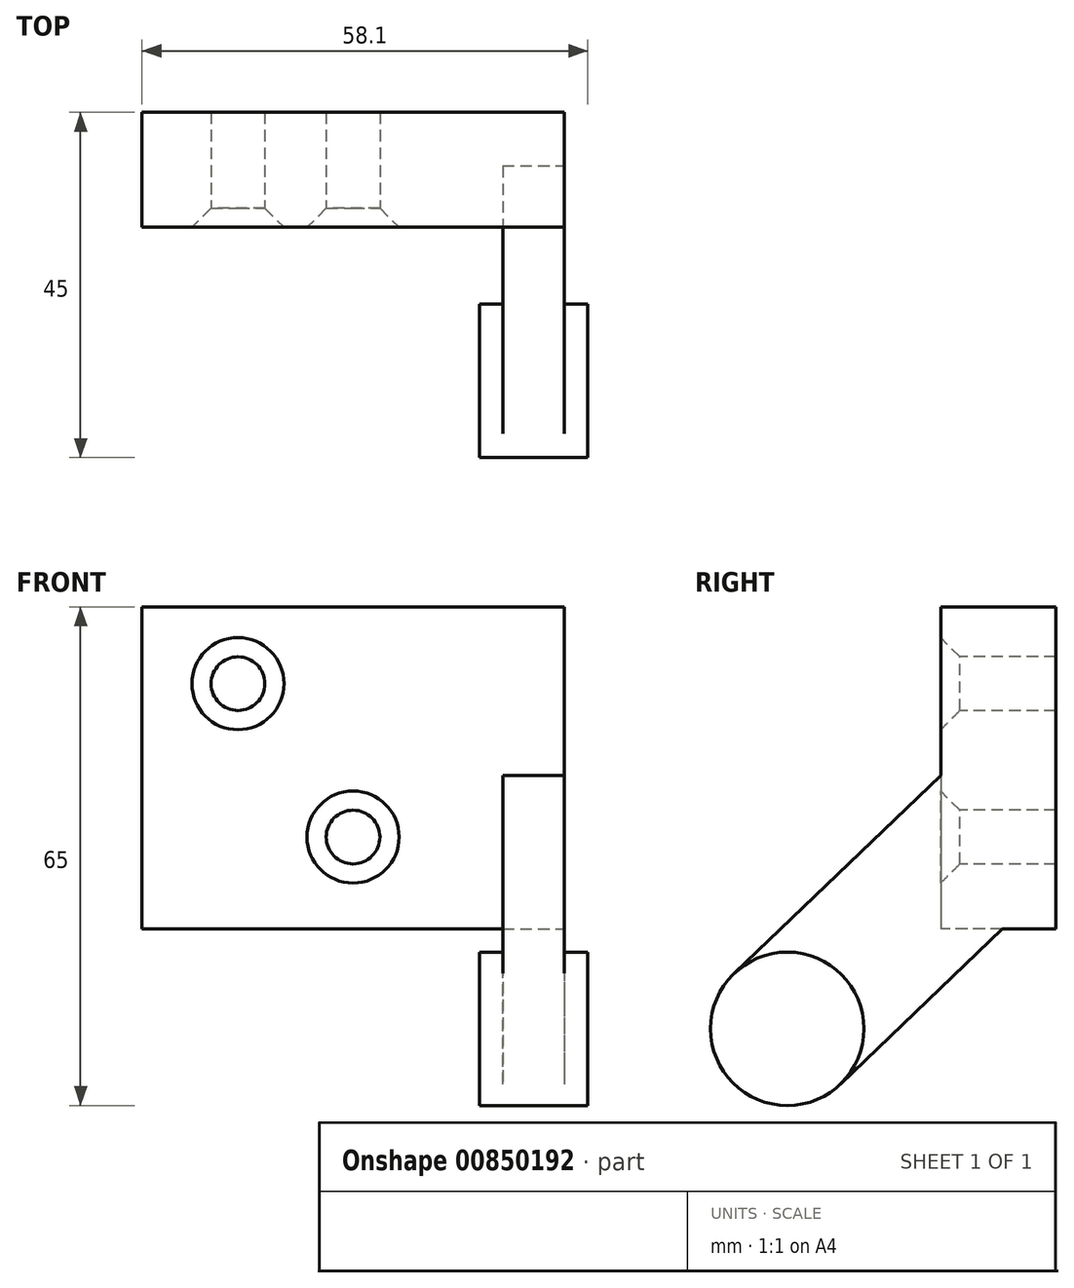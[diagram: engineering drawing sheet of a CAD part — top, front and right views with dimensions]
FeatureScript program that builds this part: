
annotation { "Feature Type Name" : "Feature", "Feature Type Description" : "" }
export const myFeature = defineFeature(function(context is Context, id is Id, definition is map)
    precondition{}
    {
        {
            var Q0;
            Q0=qCreatedBy(makeId("Front.planeOp"),FACE);
            var sketch = newSketch(context, id + "F0", { "sketchPlane" : qUnion([Q0])});
            skLineSegment(sketch, "E0.bottom", {"start": v(-27.5, 0) * mm, "end": v(27.5, 0) * mm});
            skLineSegment(sketch, "E0.top", {"start": v(-27.5, -42) * mm, "end": v(27.5, -42) * mm});
            skLineSegment(sketch, "E0.left", {"start": v(-27.5, 0) * mm, "end": v(-27.5, -42) * mm});
            skLineSegment(sketch, "E0.right", {"start": v(27.5, 0) * mm, "end": v(27.5, -42) * mm});
            skSolve(sketch);
        }
        {
            var Q0;
            Q0=makeQuery(id+"F0.imprint","IMPRINT",FACE,{"disambiguationData":[TD([[makeQuery(id+"F0.imprint","IMPRINT",EDGE,{"derivedFrom":sQuery(id+"F0.wireOp",EDGE,"E0.bottom")}),-1.0]])]});
            var Q1;
            Q1=sQuery(id+"F0.wireOp",EDGE,"E0.right");
            extrude(context, id + "F1", {"entities" : qUnion([Q0]), "surfaceEntities" : qUnion([Q1]), "oppositeDirection" : true, "depth" : 15 * mm, "offsetDistance" : 25 * mm});
        }
        {
            var Q0;
            Q0=makeQuery(id+"F1.opExtrude","SWEPT_FACE",FACE,{"disambiguationData":[OSD([sQuery(id+"F0.wireOp",EDGE,"E0.right")])]});
            var sketch = newSketch(context, id + "F2", { "sketchPlane" : qUnion([Q0])});
            skLineSegment(sketch, "E1", {"start": v(0, -21.96) * mm, "end": v(-26.92, -47.78) * mm});
            skLineSegment(sketch, "E2", {"start": v(8, -42) * mm, "end": v(-13.08, -62.22) * mm});
            skLineSegment(sketch, "E3", {"start": v(-26.92, -47.78) * mm, "end": v(-13.08, -62.22) * mm});
            skCircle(sketch, "E4", {"center": v(-20, -55) * mm, "radius": 10 * mm});
            skSolve(sketch);
        }
        {
            var Q0;
            {var subQ7=sQuery(id+"F2.wireOp",EDGE,"E1");Q0=makeQuery(id+"F2.imprint","IMPRINT",FACE,{"disambiguationData":[TD([[makeQuery(id+"F2.imprint","IMPRINT",EDGE,{"derivedFrom":subQ7}),1.0]])]});}
            var Q1;
            {var subQ0=sQuery(id+"F2.wireOp",EDGE,"E3");Q1=makeQuery(id+"F2.imprint","IMPRINT",FACE,{"disambiguationData":[TD([[makeQuery(id+"F2.imprint","IMPRINT",EDGE,{"derivedFrom":subQ0}),1.0]])]});}
            extrude(context, id + "F3", {"entities" : qUnion([Q0, Q1]), "operationType" : NewBodyOperationType.ADD, "oppositeDirection" : true, "depth" : 8 * mm, "offsetDistance" : 25 * mm});
        }
        {
            var Q0;
            {var subQ0=sQuery(id+"F2.wireOp",EDGE,"E3");Q0=makeQuery(id+"F2.imprint","IMPRINT",FACE,{"disambiguationData":[TD([[makeQuery(id+"F2.imprint","IMPRINT",EDGE,{"derivedFrom":subQ0}),-1.0]])]});}
            var Q1;
            {var subQ0=sQuery(id+"F2.wireOp",EDGE,"E3");Q1=makeQuery(id+"F2.imprint","IMPRINT",FACE,{"disambiguationData":[TD([[makeQuery(id+"F2.imprint","IMPRINT",EDGE,{"derivedFrom":subQ0}),1.0]])]});}
            extrude(context, id + "F4", {"entities" : qUnion([Q0, Q1]), "operationType" : NewBodyOperationType.ADD, "depth" : 3.1 * mm, "offsetDistance" : 25 * mm, "hasSecondDirection" : true, "secondDirectionOppositeDirection" : true, "secondDirectionDepth" : 11 * mm});
        }
        {
            var Q0;
            Q0=makeQuery(id+"F1.opExtrude","CAP_FACE",FACE,{"disambiguationData":[OSD([sQuery(id+"F0.wireOp",EDGE,"E0.bottom"),sQuery(id+"F0.wireOp",EDGE,"E0.top"),sQuery(id+"F0.wireOp",EDGE,"E0.left"),sQuery(id+"F0.wireOp",EDGE,"E0.right")])],"isStart":true});
            var sketch = newSketch(context, id + "F5", { "sketchPlane" : qUnion([Q0])});
            skPoint(sketch, "E5", {"position": v(-15, -10) * mm});
            skPoint(sketch, "E6", {"position": v(0, -30) * mm});
            skSolve(sketch);
        }
        {
            var Q0;
            Q0=sQuery(id+"F5.wireOp",VERTEX,"E5");
            var Q1;
            Q1=sQuery(id+"F5.wireOp",VERTEX,"E6");
            var Q2;
            Q2=makeQuery(id+"F1.opExtrude","SWEPT_BODY",BODY,{"disambiguationData":[OSD([sQuery(id+"F0.wireOp",EDGE,"E0.bottom"),sQuery(id+"F0.wireOp",EDGE,"E0.top"),sQuery(id+"F0.wireOp",EDGE,"E0.left"),sQuery(id+"F0.wireOp",EDGE,"E0.right")])]});
            hole(context, id + "F6", {"style" : HoleStyle.C_SINK, "endStyle" : HoleEndStyle.THROUGH, "holeDiameter" : 7 * mm, "cSinkDiameter" : 12 * mm, "cSinkAngle" : 90 * degree, "majorDiameter" : 5 * mm, "isTappedThrough" : true, "tappedDepth" : 12 * mm, "tapClearance" : 3, "locations" : qUnion([Q0, Q1]), "scope" : qUnion([Q2])});
        }
    });
